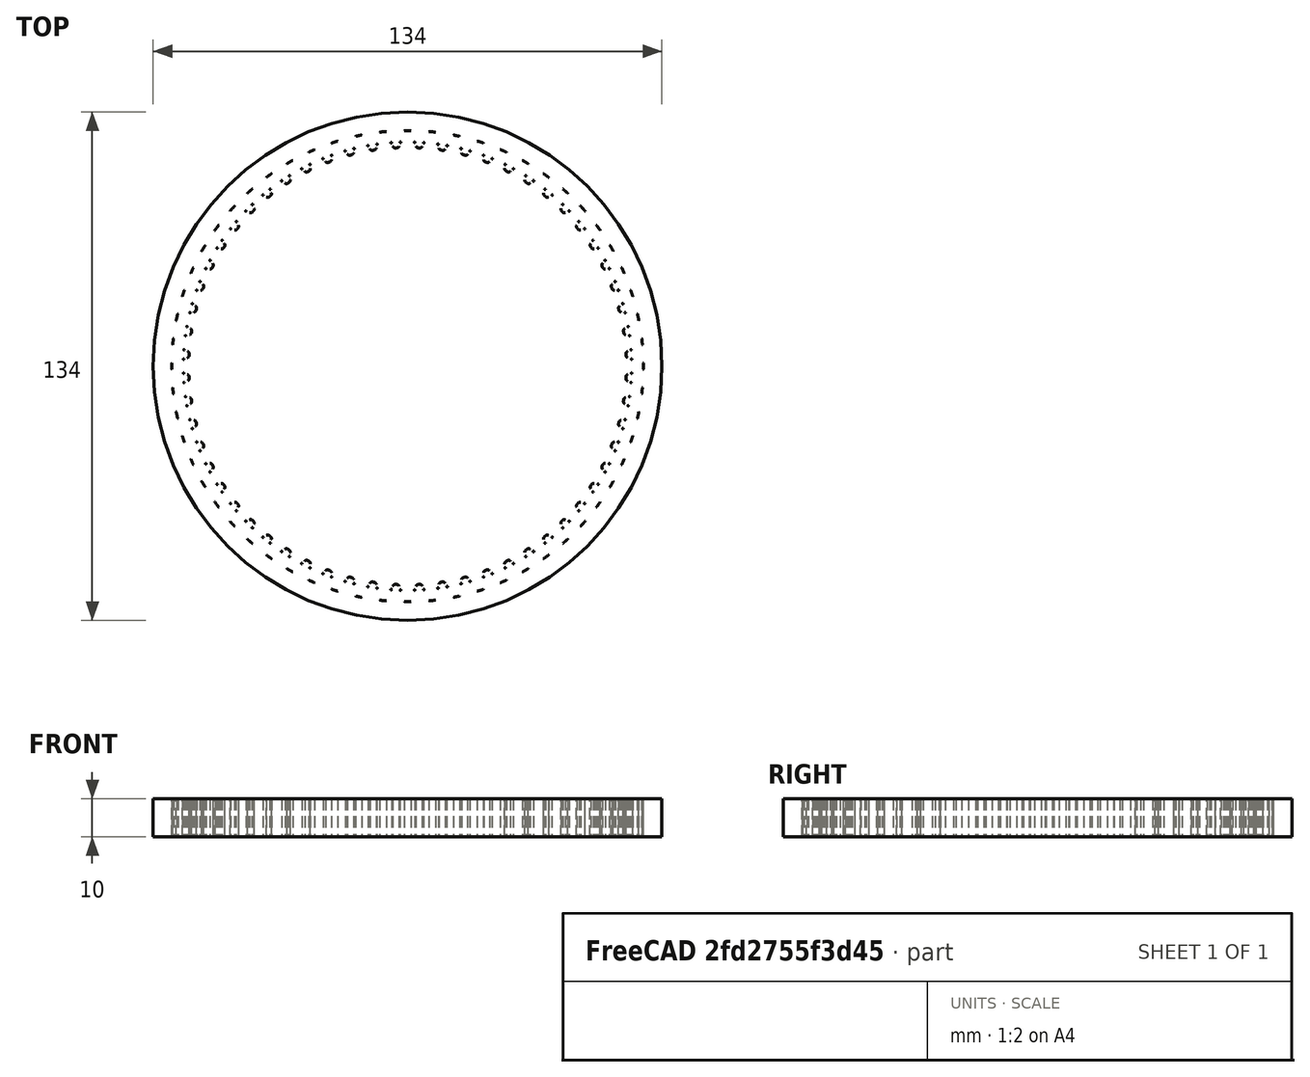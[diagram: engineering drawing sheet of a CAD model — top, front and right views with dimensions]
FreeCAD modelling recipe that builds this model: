
FCSTD DOCUMENT  (FreeCAD 0.19R24276 (Git))
Label: gear_in
License: All rights reserved
LicenseURL: http://en.wikipedia.org/wiki/All_rights_reserved
objects: Part::Part2DObjectPython×1, PartDesign::Body×1, Part::Offset2D×1, Part::Extrusion×1, Part::Cylinder×1, Part::Cut×1
note: 6 computed .brp shape members not serialized (recipe doc carries the construction recipe); baked Part::Feature solids carry a one-line shape summary decoded from their .brp

FEATURE [Part::Part2DObjectPython] InvoluteGear  # Draft 2D object (typed FeaturePython)
  ExternalGear = true
  HighPrecision = true
  Modules = 2
  NumberOfTeeth = 60
  PressureAngle = 20
FEATURE [PartDesign::Body] Body  label="Body_in_gear"
  Group = -> [InvoluteGear]
  Origin = -> Origin
FEATURE [Part::Offset2D] Offset2D
  Fill = false
  Intersection = false
  Join = 0
  Mode = 1
  SelfIntersection = false
  Source = -> InvoluteGear
  Value = 0.1
FEATURE [Part::Extrusion] Extrude
  Base = -> Offset2D
  Dir = (0,0,-1)
  DirMode = 2
  FaceMakerClass = Part::FaceMakerBullseye
  LengthFwd = 10
  LengthRev = 0
  Solid = true
  Symmetric = false
FEATURE [Part::Cylinder] Cylinder  label="Цилиндр"
  Angle = 360
  AttacherType = Attacher::AttachEngine3D
  Height = 10
  Placement = pos=(0,0,-10) rot=(0,0,1;0rad)
  Radius = 67
FEATURE [Part::Cut] Cut
  Base = -> Cylinder
  Tool = -> Extrude
